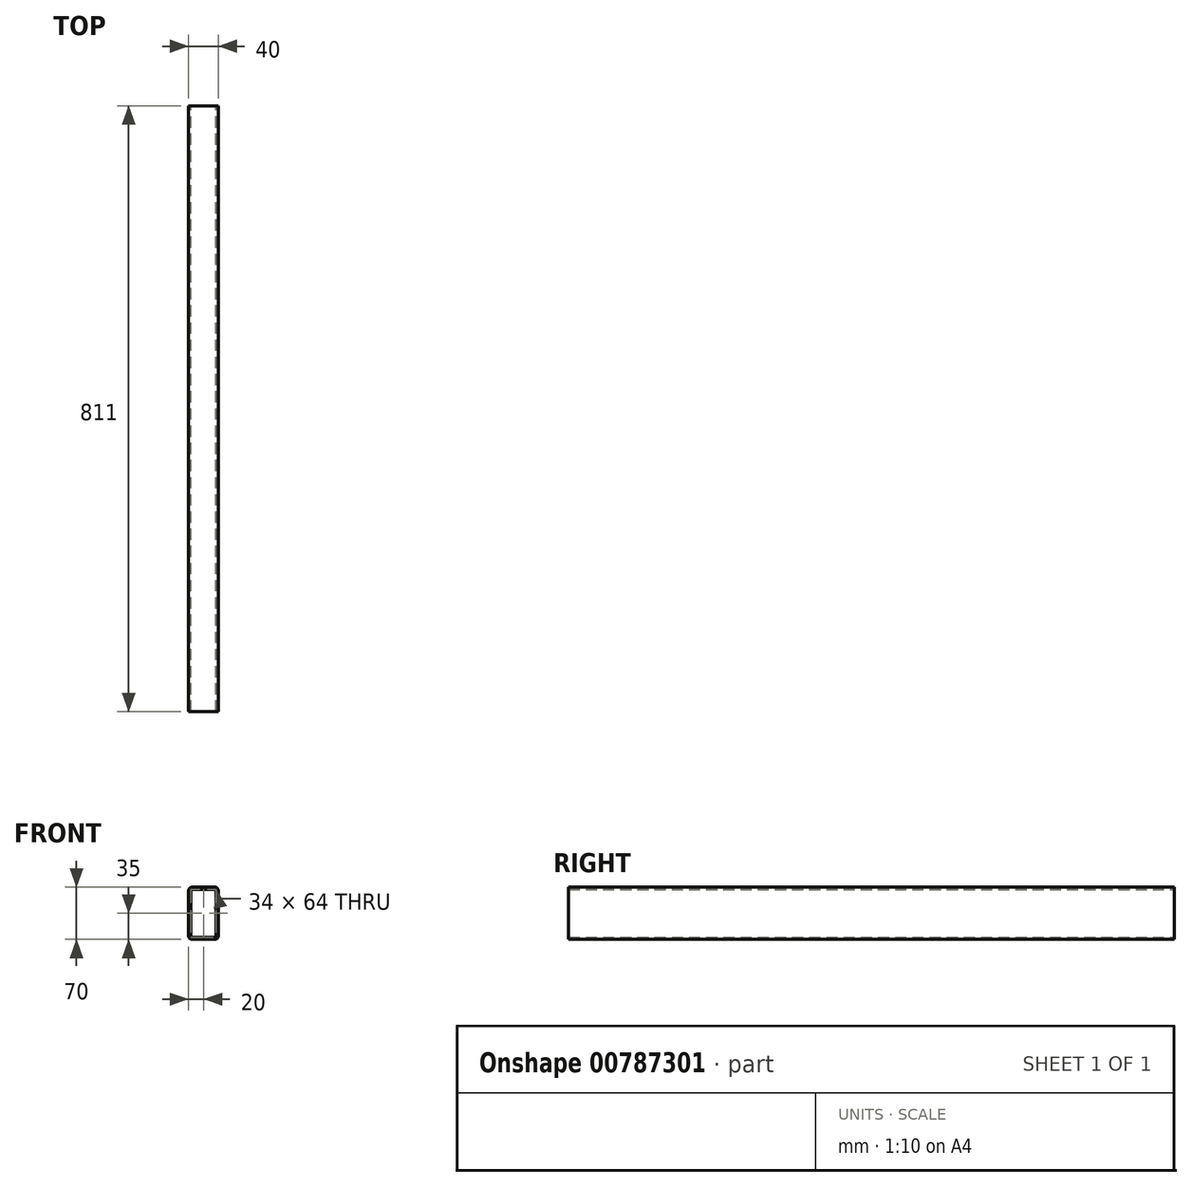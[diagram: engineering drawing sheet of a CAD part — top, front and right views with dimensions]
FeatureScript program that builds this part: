
annotation { "Feature Type Name" : "Feature", "Feature Type Description" : "" }
export const myFeature = defineFeature(function(context is Context, id is Id, definition is map)
    precondition{}
    {
        {
            var Q0;
            Q0=qCreatedBy(makeId("Front.planeOp"),FACE);
            var sketch = newSketch(context, id + "F0", { "sketchPlane" : qUnion([Q0])});
            skLineSegment(sketch, "E0.bottom", {"start": v(15, 35) * mm, "end": v(-15, 35) * mm});
            skLineSegment(sketch, "E0.top", {"start": v(15, -35) * mm, "end": v(-15, -35) * mm});
            skLineSegment(sketch, "E0.left", {"start": v(20, 30) * mm, "end": v(20, -30) * mm});
            skLineSegment(sketch, "E0.right", {"start": v(-20, 30) * mm, "end": v(-20, -30) * mm});
            skPoint(sketch, "E0.middle", {"position": v(0, 0) * mm});
            skPoint(sketch, "E1.visualSharp", {"position": v(-20, 35) * mm});
            skArc(sketch, "E1.filletArc", {"start": v(-15, 35) * mm, "mid": v(-18.54, 33.54) * mm, "end": v(-20, 30) * mm});
            skPoint(sketch, "E2.visualSharp", {"position": v(20, 35) * mm});
            skArc(sketch, "E2.filletArc", {"start": v(20, 30) * mm, "mid": v(18.54, 33.54) * mm, "end": v(15, 35) * mm});
            skPoint(sketch, "E3.visualSharp", {"position": v(20, -35) * mm});
            skArc(sketch, "E3.filletArc", {"start": v(15, -35) * mm, "mid": v(18.54, -33.54) * mm, "end": v(20, -30) * mm});
            skPoint(sketch, "E4.visualSharp", {"position": v(-20, -35) * mm});
            skArc(sketch, "E4.filletArc", {"start": v(-20, -30) * mm, "mid": v(-18.54, -33.54) * mm, "end": v(-15, -35) * mm});
            skLineSegment(sketch, "E5.0", {"start": v(-17, 32) * mm, "end": v(-17, -32) * mm});
            skLineSegment(sketch, "E5.1", {"start": v(17, 32) * mm, "end": v(-17, 32) * mm});
            skLineSegment(sketch, "E5.2", {"start": v(17, 32) * mm, "end": v(17, -32) * mm});
            skLineSegment(sketch, "E5.3", {"start": v(17, -32) * mm, "end": v(-17, -32) * mm});
            skSolve(sketch);
        }
        {
            var Q0;
            Q0=makeQuery(id+"F0.imprint","IMPRINT",FACE,{"disambiguationData":[TD([[makeQuery(id+"F0.imprint","IMPRINT",EDGE,{"derivedFrom":sQuery(id+"F0.wireOp",EDGE,"E0.bottom")}),1.0]])]});
            extrude(context, id + "F1", {"entities" : qUnion([Q0]), "depth" : (900 - 5 - 2 * (40 + 2)) * mm, "offsetDistance" : 25 * mm});
        }
    });
